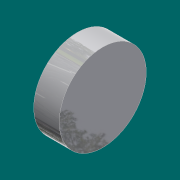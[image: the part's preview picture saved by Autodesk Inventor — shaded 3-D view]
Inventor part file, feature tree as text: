
AUTODESK INVENTOR PART (.ipt)
format: ipt  version: 2017 (Build 210142000, 142)  size: 205,312 bytes
history: native  units: mm (DEFAULTED — no unit token found)
features: other x4, revolve x1, sketch x1
ambient origin geometry x8: Origin, YZ Plane, XZ Plane, XY Plane, X Axis, Y Axis, Z Axis, Center Point
bodies: Solid1 (feature_tree)
feature tree (6):
  revolve  "Revolve1"  [1 undecoded]
  other  "Work Axis1"
  other  "Work Point1"
  other  "Work Point2"
  other  "Work Point3"
  sketch  "Sketch1"  dims[d4=90.0deg d0=48.641mm d1=5.5372mm d2=12.7mm d3=4.826mm]
note: 1 required parameter value undecoded (feature->parameter linkage not recoverable at this tier; creation-order binding heuristic only, values carry confidence <= 0.55)
